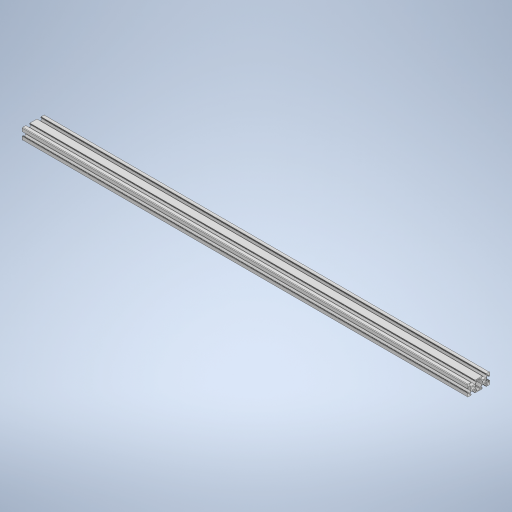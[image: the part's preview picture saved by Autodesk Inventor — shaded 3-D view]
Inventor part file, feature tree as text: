
AUTODESK INVENTOR PART (.ipt)
format: ipt  version: 2023 (Build 270158000, 158)  size: 432,640 bytes
history: native  units: mm
features: mirror x4, extrude x2, sketch x2, plane x1
ambient origin geometry x8: Origin, YZ Plane, XZ Plane, XY Plane, X Axis, Y Axis, Z Axis, Center Point
bodies: Solid1 (feature_tree)
feature tree (9):
  extrude  "Extrusion1"  Depth=10.0mm
  mirror  "Mirror1"
  mirror  "Mirror2"
  extrude  "Extrusion2"  Depth=0.5mm
  mirror  "Mirror4"
  plane  "Work Plane1"
  mirror  "Mirror5"
  sketch  "Sketch1"  dims[d1=0.5mm d2=10.0mm]
  sketch  "Sketch2"  dims[d3=5.5mm d4=3.7mm d5=2.5mm d8=10.0mm d9=1.5mm d11=6.2mm d12=135.0deg d13=1.5mm d14=800.0mm d15=0.0mm d16=135.0deg d17=90.0deg d18=0.5mm d19=0.5mm d20=1.0mm d21=1.5mm d22=10.0mm d23=11.0mm d24=7.4mm d25=6.4mm d26=10.0mm d27=800.0mm d28=0.0mm d29=0.5mm d30=0.872665mm d31=0.5mm d32=0.872665mm]
